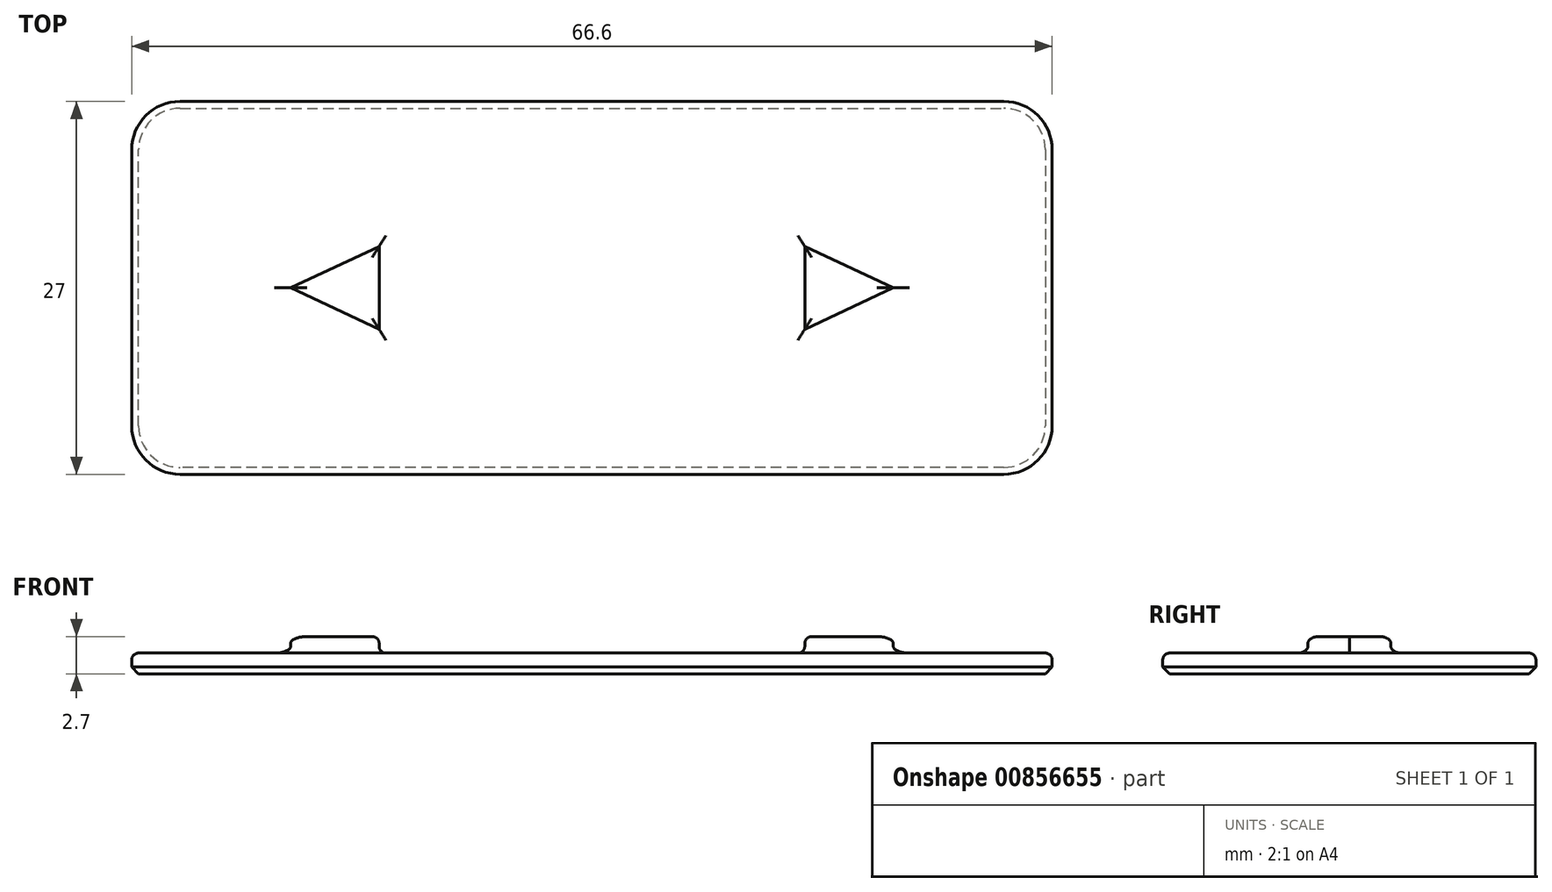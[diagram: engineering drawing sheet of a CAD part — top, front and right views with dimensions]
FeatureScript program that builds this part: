
annotation { "Feature Type Name" : "Feature", "Feature Type Description" : "" }
export const myFeature = defineFeature(function(context is Context, id is Id, definition is map)
    precondition{}
    {
        {
            var Q0;
            Q0=qCreatedBy(makeId("Top.planeOp"),FACE);
            var sketch = newSketch(context, id + "F0", { "sketchPlane" : qUnion([Q0])});
            skLineSegment(sketch, "E0.bottom", {"start": v(29.8, -13.5) * mm, "end": v(-29.8, -13.5) * mm});
            skLineSegment(sketch, "E0.top", {"start": v(29.8, 13.5) * mm, "end": v(-29.8, 13.5) * mm});
            skLineSegment(sketch, "E0.left", {"start": v(33.3, -10) * mm, "end": v(33.3, 10) * mm});
            skLineSegment(sketch, "E0.right", {"start": v(-33.3, -10) * mm, "end": v(-33.3, 10) * mm});
            skPoint(sketch, "E0.middle", {"position": v(0, 0) * mm});
            skPoint(sketch, "E1.visualSharp", {"position": v(-33.3, 13.5) * mm});
            skArc(sketch, "E1.filletArc", {"start": v(-29.8, 13.5) * mm, "mid": v(-32.27, 12.47) * mm, "end": v(-33.3, 10) * mm});
            skPoint(sketch, "E2.visualSharp", {"position": v(-33.3, -13.5) * mm});
            skArc(sketch, "E2.filletArc", {"start": v(-33.3, -10) * mm, "mid": v(-32.27, -12.47) * mm, "end": v(-29.8, -13.5) * mm});
            skPoint(sketch, "E3.visualSharp", {"position": v(33.3, -13.5) * mm});
            skArc(sketch, "E3.filletArc", {"start": v(29.8, -13.5) * mm, "mid": v(32.27, -12.47) * mm, "end": v(33.3, -10) * mm});
            skPoint(sketch, "E4.visualSharp", {"position": v(33.3, 13.5) * mm});
            skArc(sketch, "E4.filletArc", {"start": v(33.3, 10) * mm, "mid": v(32.27, 12.47) * mm, "end": v(29.8, 13.5) * mm});
            skSolve(sketch);
        }
        {
            var Q0;
            Q0=makeQuery(id+"F0.imprint","IMPRINT",FACE,{"disambiguationData":[TD([[makeQuery(id+"F0.imprint","IMPRINT",EDGE,{"derivedFrom":sQuery(id+"F0.wireOp",EDGE,"E0.bottom")}),-1.0]])]});
            extrude(context, id + "F1", {"entities" : qUnion([Q0]), "depth" : 1.5 * mm, "offsetDistance" : 25 * mm});
        }
        {
            var Q0;
            Q0=makeQuery(id+"F1.opExtrude","CAP_FACE",FACE,{"disambiguationData":[OSD([sQuery(id+"F0.wireOp",EDGE,"E0.bottom"),sQuery(id+"F0.wireOp",EDGE,"E0.top"),sQuery(id+"F0.wireOp",EDGE,"E0.left"),sQuery(id+"F0.wireOp",EDGE,"E0.right"),sQuery(id+"F0.wireOp",EDGE,"E1.filletArc"),sQuery(id+"F0.wireOp",EDGE,"E2.filletArc"),sQuery(id+"F0.wireOp",EDGE,"E3.filletArc"),sQuery(id+"F0.wireOp",EDGE,"E4.filletArc")])],"isStart":false});
            var sketch = newSketch(context, id + "F2", { "sketchPlane" : qUnion([Q0])});
            skLineSegment(sketch, "E5.bottom", {"start": v(-15.4, 3) * mm, "end": v(-21.8, 3) * mm, "construction": true});
            skLineSegment(sketch, "E5.top", {"start": v(-15.4, -3) * mm, "end": v(-21.8, -3) * mm, "construction": true});
            skLineSegment(sketch, "E5.left", {"start": v(-15.4, 3) * mm, "end": v(-15.4, -3) * mm});
            skLineSegment(sketch, "E5.right", {"start": v(-21.8, 3) * mm, "end": v(-21.8, -3) * mm, "construction": true});
            skPoint(sketch, "E5.middle", {"position": v(-18.6, 0) * mm});
            skLineSegment(sketch, "E6", {"start": v(0, 13.5) * mm, "end": v(0, -13.5) * mm, "construction": true});
            skLineSegment(sketch, "E7", {"start": v(-15.4, 3) * mm, "end": v(-21.8, 0) * mm});
            skLineSegment(sketch, "E8", {"start": v(-21.8, 0) * mm, "end": v(-15.4, -3) * mm});
            skLineSegment(sketch, "E9.MirrorCS", {"start": v(15.4, 3) * mm, "end": v(15.4, -3) * mm});
            skLineSegment(sketch, "E10.MirrorCS", {"start": v(15.4, 3) * mm, "end": v(21.8, 0) * mm});
            skLineSegment(sketch, "E11.MirrorCS", {"start": v(21.8, 0) * mm, "end": v(15.4, -3) * mm});
            skSolve(sketch);
        }
        {
            var Q0;
            Q0=makeQuery(id+"F2.imprint","IMPRINT",FACE,{"disambiguationData":[TD([[makeQuery(id+"F2.imprint","IMPRINT",EDGE,{"derivedFrom":sQuery(id+"F2.wireOp",EDGE,"E5.left")}),-1.0]])]});
            var Q1;
            Q1=makeQuery(id+"F2.imprint","IMPRINT",FACE,{"disambiguationData":[TD([[makeQuery(id+"F2.imprint","IMPRINT",EDGE,{"derivedFrom":sQuery(id+"F2.wireOp",EDGE,"E9.MirrorCS")}),1.0]])]});
            extrude(context, id + "F3", {"entities" : qUnion([Q0, Q1]), "operationType" : NewBodyOperationType.ADD, "depth" : 1.2 * mm, "offsetDistance" : 25 * mm});
        }
        {
            var Q0;
            Q0=makeQuery(id+"F1.opExtrude","CAP_FACE",FACE,{"disambiguationData":[OSD([sQuery(id+"F0.wireOp",EDGE,"E0.bottom"),sQuery(id+"F0.wireOp",EDGE,"E0.top"),sQuery(id+"F0.wireOp",EDGE,"E0.left"),sQuery(id+"F0.wireOp",EDGE,"E0.right"),sQuery(id+"F0.wireOp",EDGE,"E1.filletArc"),sQuery(id+"F0.wireOp",EDGE,"E2.filletArc"),sQuery(id+"F0.wireOp",EDGE,"E3.filletArc"),sQuery(id+"F0.wireOp",EDGE,"E4.filletArc")])],"isStart":true});
            chamfer(context, id + "F4", {"entities" : qUnion([Q0]), "width" : 0.5 * mm, "tangentPropagation" : true});
        }
        {
            var Q0;
            Q0=makeQuery(id+"F3.opExtrude","CAP_FACE",FACE,{"disambiguationData":[OSD([sQuery(id+"F2.wireOp",EDGE,"E5.left"),sQuery(id+"F2.wireOp",EDGE,"E7"),sQuery(id+"F2.wireOp",EDGE,"E8")])],"isStart":false});
            var Q1;
            Q1=makeQuery(id+"F3.opExtrude","CAP_FACE",FACE,{"disambiguationData":[OSD([sQuery(id+"F2.wireOp",EDGE,"E9.MirrorCS"),sQuery(id+"F2.wireOp",EDGE,"E10.MirrorCS"),sQuery(id+"F2.wireOp",EDGE,"E11.MirrorCS")])],"isStart":false});
            var Q2;
            Q2=makeQuery(id+"F1.opExtrude","CAP_FACE",FACE,{"disambiguationData":[OSD([sQuery(id+"F0.wireOp",EDGE,"E0.bottom"),sQuery(id+"F0.wireOp",EDGE,"E0.top"),sQuery(id+"F0.wireOp",EDGE,"E0.left"),sQuery(id+"F0.wireOp",EDGE,"E0.right"),sQuery(id+"F0.wireOp",EDGE,"E1.filletArc"),sQuery(id+"F0.wireOp",EDGE,"E2.filletArc"),sQuery(id+"F0.wireOp",EDGE,"E3.filletArc"),sQuery(id+"F0.wireOp",EDGE,"E4.filletArc")])],"isStart":false});
            fillet(context, id + "F5", {"entities" : qUnion([Q0, Q1, Q2]), "radius" : 0.5 * mm, "tangentPropagation" : true, "allowEdgeOverflow" : false});
        }
    });
